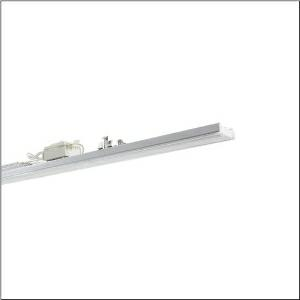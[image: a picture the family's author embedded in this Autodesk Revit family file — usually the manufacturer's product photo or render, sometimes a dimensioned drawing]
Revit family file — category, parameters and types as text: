
# Revit family: licross_11_recessed_ho_51tl12dn4exm3c
name_source: partatom
category: Lighting Fixtures
units: mm (PartAtom-declared; Revit-internal decimal feet)

## family parameters
Cut with Voids When Loaded = No
Host = Face
Light Source = No
Part Type = Normal
Room Calculation Point = No
Round Connector Dimension = Use Diameter
Shared = No

## types (1)
- --- (1 x LED, 1000 lm, 7.2 W, 4000K)
    Apparent Load = 7 VA
    CIE Flux Codes = 66 91 98 100 100
    Color Rendering = 80
    Color Temperature = 4000K
    Default Elevation = 1800 mm
    Description = Licross 11 Recessed HO, luminaire insert, of sheet steel, coil coated, white, length: 1.500mm, width: 66mm, height: 67mm, LED rated luminous flux: 14.030lm, light colour: 840, SDCM (Standard Deviation of Colour Matching)MacAdam ≤ 2 SDCM (initial), control gear: DALI 2 (for two DALI lines), with plug, 6-pole, with phase selection, for trunking rail, 14-core, mains connection: 220..240V, AC, 50/60Hz, rated input power: 81W, for trunking rail, 14-core, internal wiring halogen-free, for emergency light function, converter,control gear: single battery element, battery: LiFePO4, 9Ah, primary optical cover: cover, of PMMA, light emission: direct distribution, primary light characteristic: symmetric, protection rating (complete): IP40, insulation class (complete): insulation class I (protective earthing), certification: CE, UKCA, protection symbol: D if used in an environment without relevant dust loads with corresponding accessories, impact resistance: IK06, permissible ambient temperature for indoor applications: +5..+30°C, standard: EN 60598-2-22, LABS conformity tested according to VDMA 24364:2018-05, reducing of maximum allowable ambient temperature of 5°C with ceiling mounting, corresponds to IFS (International Featured Standards) requirements for safety and quality in the food industry, The light source and the operating device comply with the requirements of the Ecodesign Regulation (EU) 2019/2020 and are replaceable in accordance with this regulation, packaging unit: 1 piece
    Height = 58 mm
    Lamp = 1 x LED
    Lamp Light Flux = 1000 lm
    Lamp Power = 7.2 W
    Lamp count = 1
    Length = 1500 mm
    Luminous efficacy = 139 lm/W
    Manufacturer = Siteco
    ModVariant = No
    Model = 51TL12DN4EXM3C
    Mounting Place = Ceiling
    Mounting Type = Pendant
    Number of Poles = 1
    OnlyDefault = Yes
    Power Factor = 1
    Product Name = Licross 11 Recessed HO
    Product group = luminaire insert | ceiling pendant
    ProductGroupID = 901
    Protection Class = Protection class I
    Protection Degree = IP 40
    RLX_Detail_Level = 1
    RLX_Emergency_Light_Flux = 0 lm
    RLX_Emergency_Type = 0
    RLX_Emergency_Type_DB = No
    RlxData = <blob elided: 25277 chars, md5=db57aebd>
    Socket = socket
    Standby Power = 0 W
    System Light Flux = 1000 lm
    System Power = 7 W
    Type Comments = : emergency light operation: 3 h
    Type Image = l_1296930.jpg
    URL = http://relux.com
    VarID = @adj_093841
    Voltage = 0 V
    Weight = 0.00 kg
    Width = 66 mm

## geometry (parser evidence)
native form markers: Blend x4, Sweep x11
no freeform markers — native parametric forms only
